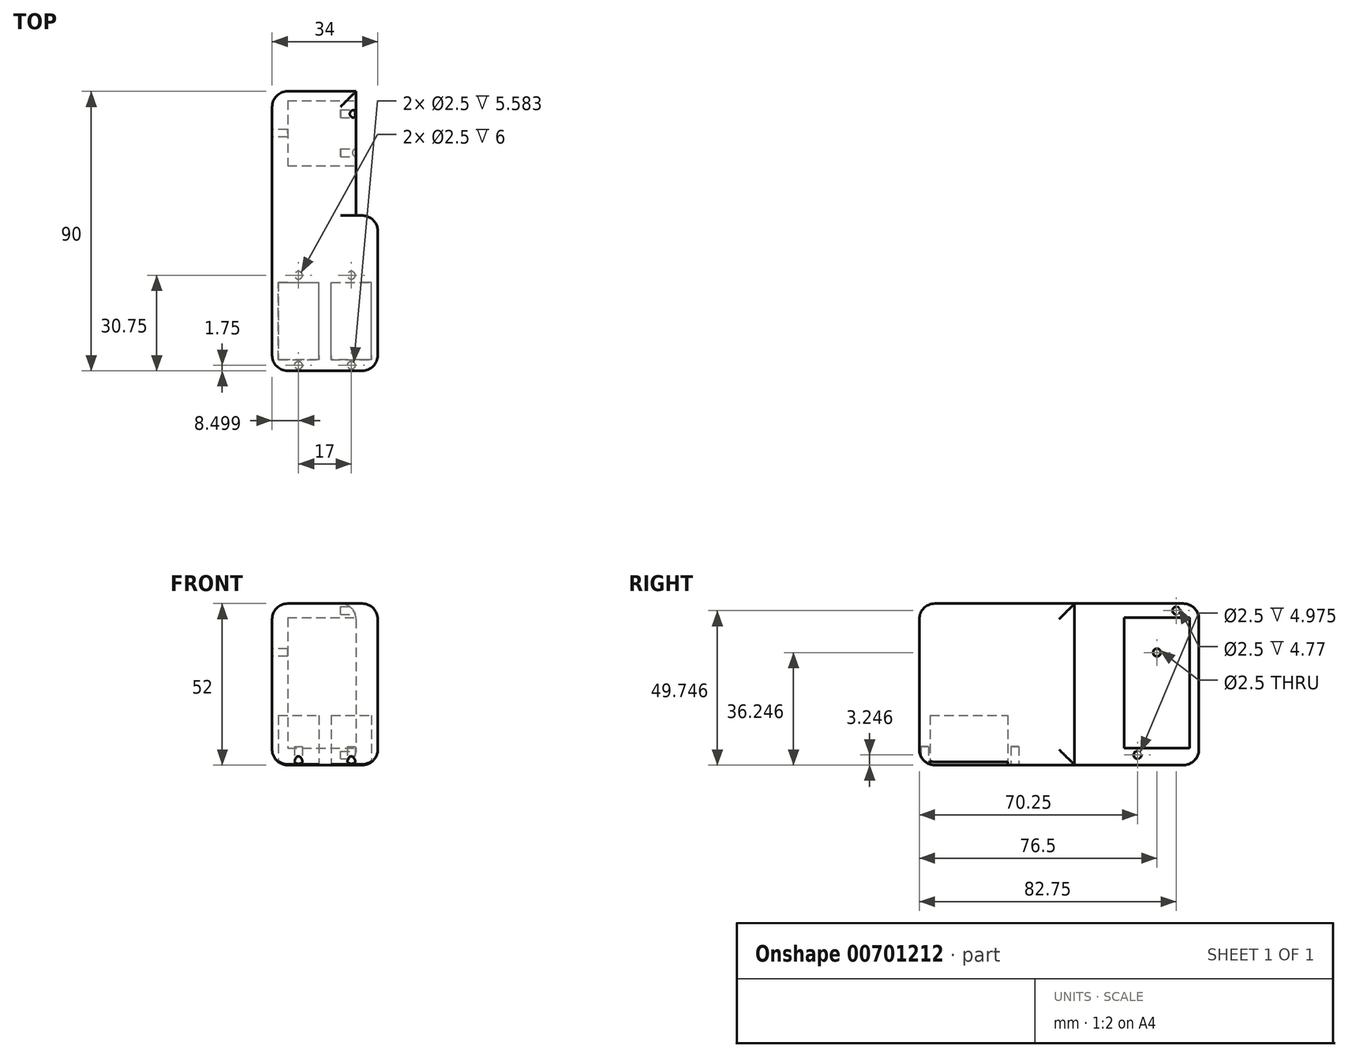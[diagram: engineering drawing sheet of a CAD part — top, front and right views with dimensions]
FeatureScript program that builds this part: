
annotation { "Feature Type Name" : "Feature", "Feature Type Description" : "" }
export const myFeature = defineFeature(function(context is Context, id is Id, definition is map)
    precondition{}
    {
        {
            var Q0;
            Q0=qCreatedBy(makeId("Front.planeOp"),FACE);
            var sketch = newSketch(context, id + "F0", { "sketchPlane" : qUnion([Q0])});
            skLineSegment(sketch, "E0.bottom", {"start": v(12.4, 37.9) * mm, "end": v(-14.6, 37.9) * mm});
            skLineSegment(sketch, "E0.top", {"start": v(12.4, -14.1) * mm, "end": v(-14.6, -14.1) * mm});
            skLineSegment(sketch, "E0.left", {"start": v(12.4, 37.9) * mm, "end": v(12.4, -14.1) * mm});
            skLineSegment(sketch, "E0.right", {"start": v(-14.6, 37.9) * mm, "end": v(-14.6, -14.1) * mm});
            skSolve(sketch);
        }
        {
            var Q0;
            Q0 = qSketchRegion(id + "F0", true);
            extrude(context, id + "F1", {"entities" : qUnion([Q0]), "depth" : 40 * mm, "offsetDistance" : 25 * mm});
        }
        {
            var Q0;
            Q0=makeQuery(id+"F1.opExtrude","SWEPT_FACE",FACE,{"disambiguationData":[OSD([sQuery(id+"F0.wireOp",EDGE,"E0.left")])]});
            var sketch = newSketch(context, id + "F2", { "sketchPlane" : qUnion([Q0])});
            skLineSegment(sketch, "E1.bottom", {"start": v(-3, 33.4) * mm, "end": v(-24, 33.4) * mm});
            skLineSegment(sketch, "E1.top", {"start": v(-3, -8.6) * mm, "end": v(-24, -8.6) * mm});
            skLineSegment(sketch, "E1.left", {"start": v(-3, 33.4) * mm, "end": v(-3, -8.6) * mm});
            skLineSegment(sketch, "E1.right", {"start": v(-24, 33.4) * mm, "end": v(-24, -8.6) * mm});
            skSolve(sketch);
        }
        {
            var Q0;
            Q0 = qSketchRegion(id + "F2", true);
            extrude(context, id + "F3", {"entities" : qUnion([Q0]), "operationType" : NewBodyOperationType.REMOVE, "oppositeDirection" : true, "depth" : 22 * mm, "offsetDistance" : 25 * mm});
        }
        {
            var Q0;
            Q0=makeQuery(id+"F1.opExtrude","SWEPT_FACE",FACE,{"disambiguationData":[OSD([sQuery(id+"F0.wireOp",EDGE,"E0.left")])]});
            var sketch = newSketch(context, id + "F4", { "sketchPlane" : qUnion([Q0])});
            skPoint(sketch, "E2.centerSnap0", {"position": v(-13.5, -8.6) * mm});
            skCircle(sketch, "E3", {"center": v(-7.25, 35.66) * mm, "radius": 1.25 * mm});
            skCircle(sketch, "E4", {"center": v(-19.75, -10.84) * mm, "radius": 1.25 * mm});
            skSolve(sketch);
        }
        {
            var Q0;
            Q0 = qSketchRegion(id + "F4", true);
            extrude(context, id + "F5", {"entities" : qUnion([Q0]), "operationType" : NewBodyOperationType.REMOVE, "oppositeDirection" : true, "depth" : 5 * mm, "offsetDistance" : 25 * mm});
        }
        {
            var Q0;
            Q0=makeQuery(id+"F1.opExtrude","SWEPT_FACE",FACE,{"disambiguationData":[OSD([sQuery(id+"F0.wireOp",EDGE,"E0.right")])]});
            var sketch = newSketch(context, id + "F6", { "sketchPlane" : qUnion([Q0])});
            skCircle(sketch, "E5", {"center": v(13.5, 22.16) * mm, "radius": 1.25 * mm});
            skSolve(sketch);
        }
        {
            var Q0;
            Q0 = qSketchRegion(id + "F6", true);
            extrude(context, id + "F7", {"entities" : qUnion([Q0]), "operationType" : NewBodyOperationType.REMOVE, "oppositeDirection" : true, "depth" : 6 * mm, "offsetDistance" : 25 * mm});
        }
        {
            var Q0;
            Q0=makeQuery(id+"F1.opExtrude","CAP_FACE",FACE,{"disambiguationData":[OSD([sQuery(id+"F0.wireOp",EDGE,"E0.bottom"),sQuery(id+"F0.wireOp",EDGE,"E0.top"),sQuery(id+"F0.wireOp",EDGE,"E0.left"),sQuery(id+"F0.wireOp",EDGE,"E0.right")])],"isStart":false});
            var sketch = newSketch(context, id + "F8", { "sketchPlane" : qUnion([Q0])});
            skLineSegment(sketch, "E6.bottom", {"start": v(-14.6, 37.9) * mm, "end": v(19.4, 37.9) * mm});
            skLineSegment(sketch, "E6.top", {"start": v(-14.6, -14.1) * mm, "end": v(19.4, -14.1) * mm});
            skLineSegment(sketch, "E6.left", {"start": v(-14.6, 37.9) * mm, "end": v(-14.6, -14.1) * mm});
            skLineSegment(sketch, "E6.right", {"start": v(19.4, 37.9) * mm, "end": v(19.4, -14.1) * mm});
            skSolve(sketch);
        }
        {
            var Q0;
            Q0 = qSketchRegion(id + "F8", true);
            extrude(context, id + "F9", {"entities" : qUnion([Q0]), "operationType" : NewBodyOperationType.ADD, "depth" : 50 * mm, "offsetDistance" : 25 * mm});
        }
        {
            var Q0;
            Q0=makeQuery(id+"F9.boolean.opBoolean","MERGE",FACE,{"derivedFrom":[makeQuery(id+"F1.opExtrude","SWEPT_FACE",FACE,{"disambiguationData":[OSD([sQuery(id+"F0.wireOp",EDGE,"E0.top")])]}),makeQuery(id+"F9.opExtrude","SWEPT_FACE",FACE,{"disambiguationData":[OSD([sQuery(id+"F8.wireOp",EDGE,"E6.top")])]})]});
            var sketch = newSketch(context, id + "F10", { "sketchPlane" : qUnion([Q0])});
            skLineSegment(sketch, "E7.bottom", {"start": v(-12.6, 86.5) * mm, "end": v(0.4, 86.5) * mm});
            skLineSegment(sketch, "E7.top", {"start": v(-12.6, 61.5) * mm, "end": v(0.4, 61.5) * mm});
            skLineSegment(sketch, "E7.left", {"start": v(-12.6, 86.5) * mm, "end": v(-12.6, 61.5) * mm});
            skLineSegment(sketch, "E7.right", {"start": v(0.4, 86.5) * mm, "end": v(0.4, 61.5) * mm});
            skLineSegment(sketch, "E8.bottom", {"start": v(4.4, 86.5) * mm, "end": v(17.4, 86.5) * mm});
            skLineSegment(sketch, "E8.top", {"start": v(4.4, 61.5) * mm, "end": v(17.4, 61.5) * mm});
            skLineSegment(sketch, "E8.left", {"start": v(4.4, 86.5) * mm, "end": v(4.4, 61.5) * mm});
            skLineSegment(sketch, "E8.right", {"start": v(17.4, 86.5) * mm, "end": v(17.4, 61.5) * mm});
            skSolve(sketch);
        }
        {
            var Q0;
            Q0 = qSketchRegion(id + "F10", true);
            extrude(context, id + "F11", {"entities" : qUnion([Q0]), "operationType" : NewBodyOperationType.REMOVE, "oppositeDirection" : true, "depth" : 16 * mm, "offsetDistance" : 25 * mm});
        }
        {
            var Q0;
            Q0=makeQuery(id+"F9.boolean.opBoolean","MERGE",FACE,{"derivedFrom":[makeQuery(id+"F1.opExtrude","SWEPT_FACE",FACE,{"disambiguationData":[OSD([sQuery(id+"F0.wireOp",EDGE,"E0.top")])]}),makeQuery(id+"F9.opExtrude","SWEPT_FACE",FACE,{"disambiguationData":[OSD([sQuery(id+"F8.wireOp",EDGE,"E6.top")])]})]});
            var sketch = newSketch(context, id + "F12", { "sketchPlane" : qUnion([Q0])});
            skCircle(sketch, "E9", {"center": v(-6.1, 88.25) * mm, "radius": 1.25 * mm});
            skCircle(sketch, "E10", {"center": v(10.9, 88.25) * mm, "radius": 1.25 * mm});
            skCircle(sketch, "E11", {"center": v(-6.1, 59.25) * mm, "radius": 1.25 * mm});
            skCircle(sketch, "E12", {"center": v(10.9, 59.25) * mm, "radius": 1.25 * mm});
            skSolve(sketch);
        }
        {
            var Q0;
            Q0 = qSketchRegion(id + "F12", true);
            extrude(context, id + "F13", {"entities" : qUnion([Q0]), "operationType" : NewBodyOperationType.REMOVE, "oppositeDirection" : true, "depth" : 6 * mm, "offsetDistance" : 25 * mm});
        }
        {
            var Q0;
            Q0=makeQuery(id+"F9.opExtrude","SWEPT_EDGE",EDGE,{"disambiguationData":[OSD([sQuery(id+"F8.wireOp",EDGE,"E6.top"),sQuery(id+"F8.wireOp",EDGE,"E6.right")])]});
            var Q1;
            Q1=makeQuery(id+"F9.opExtrude","SWEPT_EDGE",EDGE,{"disambiguationData":[OSD([sQuery(id+"F8.wireOp",EDGE,"E6.bottom"),sQuery(id+"F8.wireOp",EDGE,"E6.right")])]});
            var Q2;
            Q2=makeQuery(id+"F9.opExtrude","CAP_EDGE",EDGE,{"disambiguationData":[OSD([sQuery(id+"F8.wireOp",EDGE,"E6.right")])],"isStart":true});
            var Q3;
            Q3=makeQuery(id+"F1.opExtrude","SWEPT_EDGE",EDGE,{"disambiguationData":[OSD([sQuery(id+"F0.wireOp",EDGE,"E0.top"),sQuery(id+"F0.wireOp",EDGE,"E0.left")])]});
            var Q4;
            Q4=makeQuery(id+"F1.opExtrude","SWEPT_EDGE",EDGE,{"disambiguationData":[OSD([sQuery(id+"F0.wireOp",EDGE,"E0.bottom"),sQuery(id+"F0.wireOp",EDGE,"E0.left")])]});
            var Q5;
            Q5=makeQuery(id+"F9.boolean.opBoolean","MERGE",EDGE,{"derivedFrom":[makeQuery(id+"F1.opExtrude","SWEPT_EDGE",EDGE,{"disambiguationData":[OSD([sQuery(id+"F0.wireOp",EDGE,"E0.top"),sQuery(id+"F0.wireOp",EDGE,"E0.right")])]}),makeQuery(id+"F9.opExtrude","SWEPT_EDGE",EDGE,{"disambiguationData":[OSD([sQuery(id+"F8.wireOp",EDGE,"E6.top"),sQuery(id+"F8.wireOp",EDGE,"E6.left")])]})]});
            var Q6;
            Q6=makeQuery(id+"F1.opExtrude","CAP_EDGE",EDGE,{"disambiguationData":[OSD([sQuery(id+"F0.wireOp",EDGE,"E0.top")])],"isStart":true});
            var Q7;
            Q7=makeQuery(id+"F9.opExtrude","CAP_EDGE",EDGE,{"disambiguationData":[OSD([sQuery(id+"F8.wireOp",EDGE,"E6.top")])],"isStart":false});
            var Q8;
            Q8=makeQuery(id+"F1.opExtrude","CAP_EDGE",EDGE,{"disambiguationData":[OSD([sQuery(id+"F0.wireOp",EDGE,"E0.bottom")])],"isStart":true});
            var Q9;
            Q9=makeQuery(id+"F1.opExtrude","CAP_EDGE",EDGE,{"disambiguationData":[OSD([sQuery(id+"F0.wireOp",EDGE,"E0.right")])],"isStart":true});
            var Q10;
            Q10=makeQuery(id+"F9.boolean.opBoolean","MERGE",EDGE,{"derivedFrom":[makeQuery(id+"F1.opExtrude","SWEPT_EDGE",EDGE,{"disambiguationData":[OSD([sQuery(id+"F0.wireOp",EDGE,"E0.bottom"),sQuery(id+"F0.wireOp",EDGE,"E0.right")])]}),makeQuery(id+"F9.opExtrude","SWEPT_EDGE",EDGE,{"disambiguationData":[OSD([sQuery(id+"F8.wireOp",EDGE,"E6.bottom"),sQuery(id+"F8.wireOp",EDGE,"E6.left")])]})]});
            var Q11;
            Q11=makeQuery(id+"F9.opExtrude","CAP_EDGE",EDGE,{"disambiguationData":[OSD([sQuery(id+"F8.wireOp",EDGE,"E6.bottom")])],"isStart":false});
            fillet(context, id + "F14", {"entities" : qUnion([Q0, Q1, Q2, Q3, Q4, Q5, Q6, Q7, Q8, Q9, Q10, Q11]), "radius" : 5 * mm, "tangentPropagation" : true, "allowEdgeOverflow" : false});
        }
        {
            var Q0;
            Q0=makeQuery(id+"F9.opExtrude","CAP_EDGE",EDGE,{"disambiguationData":[OSD([sQuery(id+"F8.wireOp",EDGE,"E6.right")])],"isStart":false});
            var Q1;
            Q1=makeQuery(id+"F9.opExtrude","CAP_EDGE",EDGE,{"disambiguationData":[OSD([sQuery(id+"F8.wireOp",EDGE,"E6.left")])],"isStart":false});
            fillet(context, id + "F15", {"entities" : qUnion([Q0, Q1]), "radius" : 5 * mm, "tangentPropagation" : true, "allowEdgeOverflow" : false});
        }
    });
